# Revit family: Фильтр К прямоугольный Naveka
name_source: partatom
category: Арматура воздуховодов
units: mm (PartAtom-declared; Revit-internal decimal feet)

## family parameters
Всегда вертикально = Да
Заголовок OmniClass = Climate Control (HVAC)
На основе рабочей плоскости = Нет
Номер OmniClass = 23.75.00.00
Общий = Нет
При загрузке вырезать с полостями = Нет
Размер круглого соединителя = Использовать диаметр
Тип детали = Вставляется

## types (16) — shared parameters
ADSK_Единица измерения = шт.
ADSK_Завод-изготовитель = Naveka
ADSK_Наименование = Корпус компактного фильтра прямоугольного
Материал = RAL 0000 Серый металл
zero-valued in all types: ADSK_Масса

## per-type parameters (varying)
| type | A | ADSK_Марка | B | L | s |
| К-4020 компакт | 400 мм | К-4020 компакт | 200 мм | 200 мм | 20 мм |
| К-4020 | 400 мм | К-4020 компакт | 200 мм | 500 мм | 20 мм |
| К-5025 компакт | 500 мм | К-5025 компакт | 250 мм | 200 мм | 20 мм |
| К-5025 | 500 мм | К-5025 компакт | 250 мм | 530 мм | 20 мм |
| К-5030 компакт | 500 мм | К-5030 компакт | 300 мм | 200 мм | 20 мм |
| К-5030 | 500 мм | К-5030 | 300 мм | 560 мм | 20 мм |
| К-6030 компакт | 600 мм | К-6030 компакт | 300 мм | 200 мм | 20 мм |
| К-6030 | 600 мм | К-6030 | 300 мм | 650 мм | 20 мм |
| К-6035 компакт | 600 мм | К-6035 компакт | 350 мм | 200 мм | 20 мм |
| К-6035 | 600 мм | К-6035 | 350 мм | 715 мм | 20 мм |
| К-7040 компакт | 700 мм | К-7040 компакт | 400 мм | 200 мм | 30 мм |
| К-7040 | 700 мм | К-7040 | 400 мм | 785 мм | 30 мм |
| К-8050 компакт | 800 мм | К-8050 компакт | 500 мм | 200 мм | 30 мм |
| К-8050 | 800 мм | К-8050 | 500 мм | 880 мм | 30 мм |
| К-10050 компакт | 1000 мм | К-10050 компакт | 500 мм | 200 мм | 30 мм |
| К-10050 | 1000 мм | К-10050 | 500 мм | 880 мм | 30 мм |
